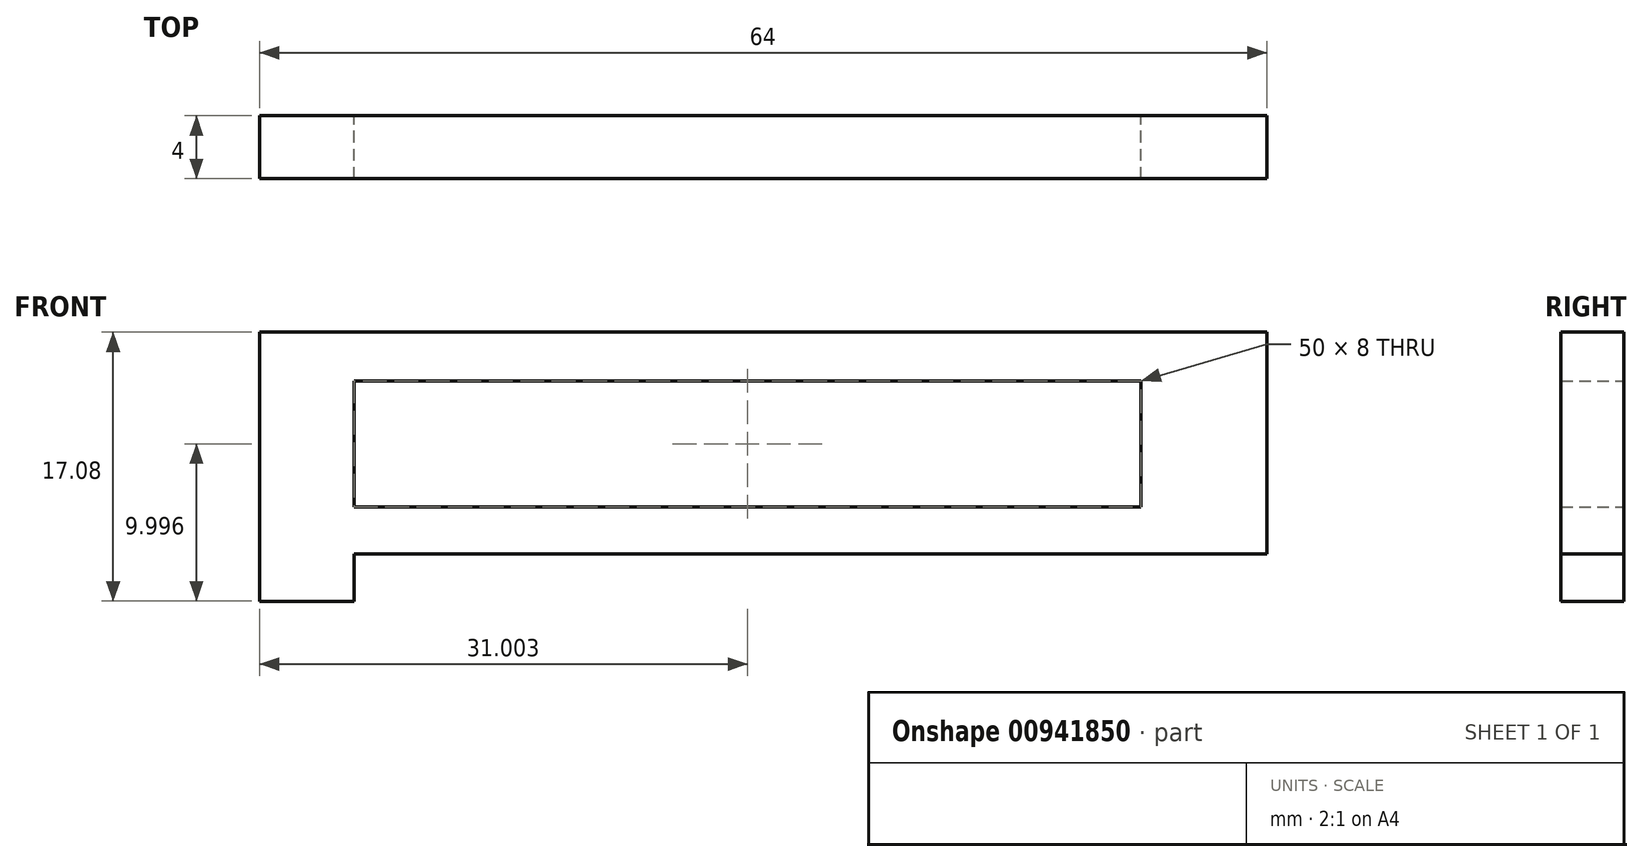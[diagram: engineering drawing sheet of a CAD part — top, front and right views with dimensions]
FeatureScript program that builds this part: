
annotation { "Feature Type Name" : "Feature", "Feature Type Description" : "" }
export const myFeature = defineFeature(function(context is Context, id is Id, definition is map)
    precondition{}
    {
        {
            var Q0;
            Q0=qCreatedBy(makeId("Front.planeOp"),FACE);
            var sketch = newSketch(context, id + "F0", { "sketchPlane" : qUnion([Q0])});
            skLineSegment(sketch, "E0.bottom", {"start": v(32, 8.54) * mm, "end": v(-32, 8.54) * mm});
            skLineSegment(sketch, "E0.right", {"start": v(-32, 8.54) * mm, "end": v(-32, -8.54) * mm});
            skPoint(sketch, "E0.middle", {"position": v(0, 0) * mm});
            skLineSegment(sketch, "E1", {"start": v(-26, 5.46) * mm, "end": v(24, 5.46) * mm});
            skLineSegment(sketch, "E2", {"start": v(-26, -5.54) * mm, "end": v(-26, 5.46) * mm});
            skLineSegment(sketch, "E3", {"start": v(24, 5.46) * mm, "end": v(24, -2.54) * mm});
            skLineSegment(sketch, "E4", {"start": v(-26, -2.54) * mm, "end": v(24, -2.54) * mm});
            skLineSegment(sketch, "E5", {"start": v(32, 8.54) * mm, "end": v(32, -5.54) * mm});
            skLineSegment(sketch, "E6", {"start": v(-26, -5.54) * mm, "end": v(32, -5.54) * mm});
            skLineSegment(sketch, "E7", {"start": v(-32, -8.54) * mm, "end": v(-26, -8.54) * mm});
            skLineSegment(sketch, "E8", {"start": v(-26, -5.54) * mm, "end": v(-26, -8.54) * mm});
            skSolve(sketch);
        }
        {
            var Q0;
            Q0=makeQuery(id+"F0.imprint","IMPRINT",FACE,{"disambiguationData":[TD([[makeQuery(id+"F0.imprint","IMPRINT",EDGE,{"derivedFrom":sQuery(id+"F0.wireOp",EDGE,"E0.bottom")}),1.0]])]});
            extrude(context, id + "F1", {"entities" : qUnion([Q0]), "depth" : 4 * mm, "offsetDistance" : 25.4 * mm, "symmetric" : true});
        }
    });
